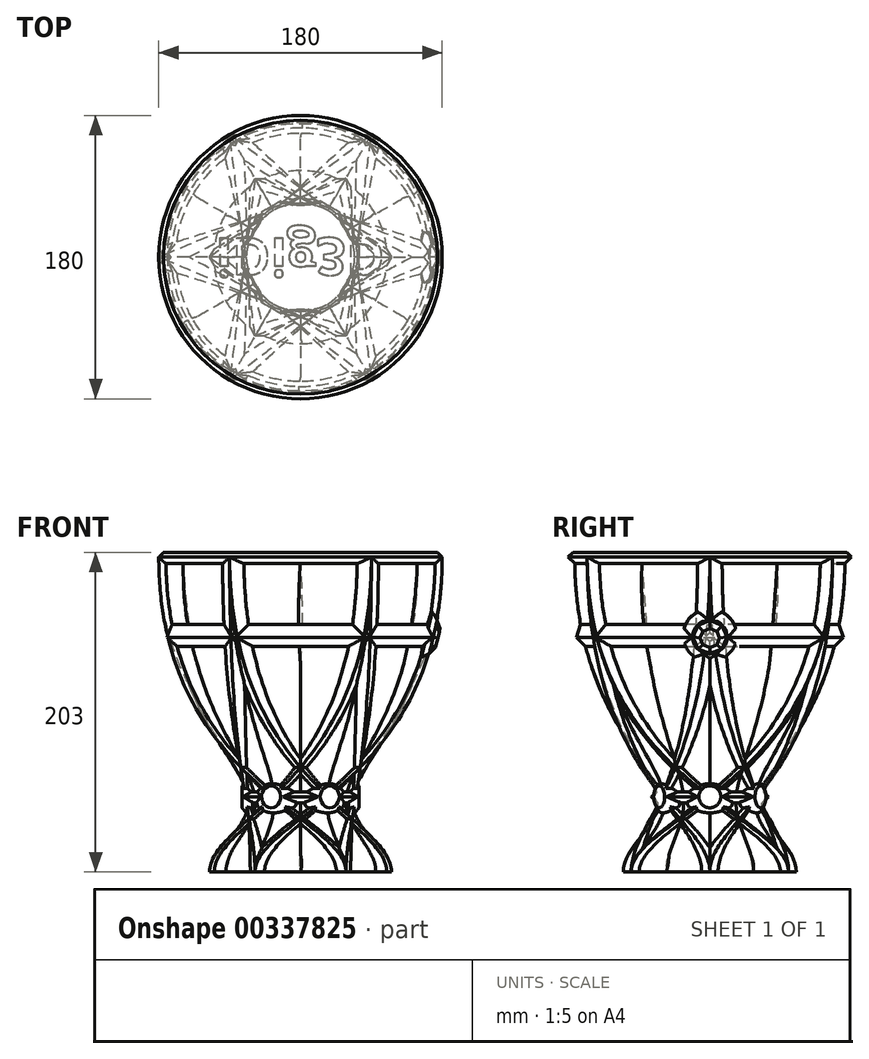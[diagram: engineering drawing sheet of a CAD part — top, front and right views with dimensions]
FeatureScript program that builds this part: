
annotation { "Feature Type Name" : "Feature", "Feature Type Description" : "" }
export const myFeature = defineFeature(function(context is Context, id is Id, definition is map)
    precondition{}
    {
        {
            var Q0;
            Q0=qCreatedBy(makeId("Top.planeOp"),FACE);
            var sketch = newSketch(context, id + "F0", { "sketchPlane" : qUnion([Q0])});
            skCircle(sketch, "E0.cCircle", {"center": v(0, 0) * mm, "radius": 50 * mm, "construction": true});
            skLineSegment(sketch, "E0.0", {"start": v(-28.87, 50) * mm, "end": v(28.87, 50) * mm});
            skLineSegment(sketch, "E0.1", {"start": v(28.87, 50) * mm, "end": v(57.74, 0) * mm});
            skLineSegment(sketch, "E0.2", {"start": v(57.74, 0) * mm, "end": v(28.87, -50) * mm});
            skLineSegment(sketch, "E0.3", {"start": v(28.87, -50) * mm, "end": v(-28.87, -50) * mm});
            skLineSegment(sketch, "E0.4", {"start": v(-28.87, -50) * mm, "end": v(-57.74, 0) * mm});
            skLineSegment(sketch, "E0.5", {"start": v(-57.74, 0) * mm, "end": v(-28.87, 50) * mm});
            skPoint(sketch, "E0.0.midPoint", {"position": v(0, 50) * mm});
            skArc(sketch, "E1", {"start": v(22.87, 50) * mm, "mid": v(0, 54.98) * mm, "end": v(-22.87, 50) * mm});
            skArc(sketch, "E2.1.0", {"start": v(-31.87, 44.8) * mm, "mid": v(-47.62, 27.5) * mm, "end": v(-54.74, 5.2) * mm});
            skArc(sketch, "E2.2.0", {"start": v(-54.74, -5.2) * mm, "mid": v(-47.62, -27.5) * mm, "end": v(-31.87, -44.8) * mm});
            skArc(sketch, "E3.3.3.0", {"start": v(-22.87, -50) * mm, "mid": v(0, -54.98) * mm, "end": v(22.87, -50) * mm});
            skArc(sketch, "E3.3.4.0", {"start": v(31.87, -44.8) * mm, "mid": v(47.62, -27.5) * mm, "end": v(54.74, -5.2) * mm});
            skArc(sketch, "E3.3.5.0", {"start": v(54.74, 5.2) * mm, "mid": v(47.62, 27.5) * mm, "end": v(31.87, 44.8) * mm});
            skSolve(sketch);
        }
        {
            var Q0;
            Q0=qCreatedBy(makeId("Top.planeOp"),FACE);
            cPlane(context, id + "F1", {"entities" : qUnion([Q0]), "cplaneType" : CPlaneType.OFFSET, "offset" : 200 * mm, "width" : 150 * mm, "height" : 150 * mm});
        }
        {
            var Q0;
            Q0=qCreatedBy(id+"F1.planeOp",FACE);
            var sketch = newSketch(context, id + "F2", { "sketchPlane" : qUnion([Q0])});
            skCircle(sketch, "E4.cCircle", {"center": v(0, 0) * mm, "radius": 90 * mm, "construction": true});
            skLineSegment(sketch, "E4.0", {"start": v(-90, 0) * mm, "end": v(-45, 77.94) * mm});
            skLineSegment(sketch, "E4.1", {"start": v(-45, 77.94) * mm, "end": v(45, 77.94) * mm});
            skLineSegment(sketch, "E4.2", {"start": v(45, 77.94) * mm, "end": v(90, 0) * mm});
            skLineSegment(sketch, "E4.3", {"start": v(90, 0) * mm, "end": v(45, -77.94) * mm});
            skLineSegment(sketch, "E4.4", {"start": v(45, -77.94) * mm, "end": v(-45, -77.94) * mm});
            skLineSegment(sketch, "E4.5", {"start": v(-45, -77.94) * mm, "end": v(-90, 0) * mm});
            skCircle(sketch, "E5", {"center": v(0, 0) * mm, "radius": 85.85 * mm});
            skPoint(sketch, "E6", {"position": v(-85.5, 7.8) * mm});
            skSolve(sketch);
        }
        {
            var Q1;
            Q1 = qSketchRegion(id + "F0", true);
            var Q2;
            Q2 = qSketchRegion(id + "F2", true);
            var Q3;
            Q3=sQuery(id+"F0.wireOp",VERTEX,"E0.3.start");
            var Q4;
            Q4=sQuery(id+"F2.wireOp",VERTEX,"E4.0.start");
            loft(context, id + "F3", {"startCondition" : LoftEndDerivativeType.NORMAL_TO_PROFILE, "startMagnitude" : 0.5, "endCondition" : LoftEndDerivativeType.NORMAL_TO_PROFILE, "endMagnitude" : 2.1, "sheetProfilesArray" : [{ "sheetProfileEntities" : qUnion([Q1]) }, { "sheetProfileEntities" : qUnion([Q2]) }], "matchConnections" : true, "connections" : [{ "connectionEntities" : qUnion([Q3, Q4]), "connectionEdgeQueries" : qUnion([]), "connectionEdgeParameters" : [] }]});
        }
        {
            var Q0;
            {var subQ0=sQuery(id+"F2.wireOp",EDGE,"E4.5");var subQ1=sQuery(id+"F2.wireOp",EDGE,"E4.0");var subQ2=makeQuery(id+"F2.imprint","INTERSECT",VERTEX,{"derivedFrom":[subQ1,subQ0]});var subQ6=sQuery(id+"F0.wireOp",EDGE,"E1");Q0=makeQuery(id+"F3.opLoft","SWEPT_BODY",BODY,{"disambiguationData":[OSD([makeQuery(id+"F0.imprint","IMPRINT",FACE,{"disambiguationData":[TD([[makeQuery(id+"F0.imprint","IMPRINT",EDGE,{"derivedFrom":subQ6}),1.0]])]}),makeQuery(id+"F2.imprint","IMPRINT",FACE,{"disambiguationData":[TD([[makeQuery(id+"F2.imprint","IMPRINT",EDGE,{"disambiguationData":[TD([[subQ2,-1.0]])],"derivedFrom":subQ1}),-1.0]])]})])]});}
            var Q1;
            Q1=qCreatedBy(makeId("Front.planeOp"),FACE);
            mirror(context, id + "F4", {"operationType" : NewBodyOperationType.ADD, "entities" : qUnion([Q0]), "mirrorPlane" : qUnion([Q1])});
        }
        {
            var Q0;
            Q0=qCreatedBy(makeId("Front.planeOp"),FACE);
            var sketch = newSketch(context, id + "F5", { "sketchPlane" : qUnion([Q0])});
            skLineSegment(sketch, "E7", {"start": v(80.54, 160.36) * mm, "end": v(84.28, 149.21) * mm, "construction": true});
            skLineSegment(sketch, "E8", {"start": v(84.28, 149.21) * mm, "end": v(75.96, 140.9) * mm, "construction": true});
            skLineSegment(sketch, "E9", {"start": v(75.96, 140.9) * mm, "end": v(0, 158.76) * mm});
            skLineSegment(sketch, "E10", {"start": v(0, 179.3) * mm, "end": v(80.54, 160.36) * mm});
            skLineSegment(sketch, "E11", {"start": v(80, 210) * mm, "end": v(90, 200) * mm});
            skLineSegment(sketch, "E12", {"start": v(80, 190) * mm, "end": v(0, 190) * mm});
            skLineSegment(sketch, "E13", {"start": v(0, 210) * mm, "end": v(80, 210) * mm, "construction": true});
            skLineSegment(sketch, "E14", {"start": v(28.17, 56.78) * mm, "end": v(37.17, 47.78) * mm});
            skLineSegment(sketch, "E15", {"start": v(37.17, 47.78) * mm, "end": v(28.17, 38.78) * mm});
            skLineSegment(sketch, "E16", {"start": v(28.17, 38.78) * mm, "end": v(0, 38.78) * mm});
            skLineSegment(sketch, "E17", {"start": v(0, 56.78) * mm, "end": v(28.17, 56.78) * mm});
            skLineSegment(sketch, "E18.0", {"start": v(84.74, 149.1) * mm, "end": v(75.79, 140.16) * mm});
            skLineSegment(sketch, "E18.1", {"start": v(80.71, 161.1) * mm, "end": v(84.74, 149.1) * mm});
            skLineSegment(sketch, "E19", {"start": v(80.54, 160.36) * mm, "end": v(80.71, 161.1) * mm});
            skLineSegment(sketch, "E20", {"start": v(75.96, 140.9) * mm, "end": v(75.79, 140.16) * mm});
            skPoint(sketch, "E21.orphan", {"position": v(90, 200) * mm});
            skLineSegment(sketch, "E22", {"start": v(80.27, 150.15) * mm, "end": v(84.74, 149.1) * mm, "construction": true});
            skPoint(sketch, "E23.0", {"position": v(0, 247.2) * mm});
            skLineSegment(sketch, "E24", {"start": v(87, 203) * mm, "end": v(0, 203) * mm});
            skFitSpline(sketch, "E25.0", {"points": [v(-28.87, 0) * mm, v(-28.87, 33.97) * mm, v(90, 57.34) * mm, v(90, 200) * mm], "construction": true});
            skPoint(sketch, "E26.0", {"position": v(17.59, 47.78) * mm});
            skPoint(sketch, "E26.1", {"position": v(35.17, 47.78) * mm});
            skFitSpline(sketch, "E27.0", {"points": [v(85.85, 198.7) * mm, v(85.82, 195.76) * mm, v(85.67, 189.89) * mm, v(85.12, 181.1) * mm, v(84.24, 172.34) * mm, v(83.22, 165.08) * mm, v(82.21, 159.3) * mm, v(81.08, 153.56) * mm, v(79.76, 147.86) * mm, v(78.24, 142.2) * mm, v(76.59, 136.6) * mm, v(74.73, 131.06) * mm, v(72.67, 125.59) * mm, v(70.48, 120.19) * mm, v(68.1, 114.88) * mm, v(65.5, 109.67) * mm, v(62.77, 104.54) * mm, v(59.86, 99.54) * mm, v(56.76, 94.64) * mm, v(53.54, 89.84) * mm, v(50.15, 85.17) * mm, v(46.6, 80.63) * mm, v(42.93, 76.2) * mm, v(40.07, 72.97) * mm, v(38.12, 70.87) * mm], "construction": true});
            skLineSegment(sketch, "E28", {"start": v(90, 200) * mm, "end": v(80, 190) * mm});
            skLineSegment(sketch, "E29", {"start": v(0, 190) * mm, "end": v(0, 210) * mm});
            skLineSegment(sketch, "E30", {"start": v(0, 158.76) * mm, "end": v(0, 179.3) * mm});
            skLineSegment(sketch, "E31", {"start": v(0, 38.78) * mm, "end": v(0, 56.78) * mm});
            skPoint(sketch, "E32.0", {"position": v(85.5, 200) * mm});
            skPoint(sketch, "E33.0", {"position": v(38.93, 71.75) * mm});
            skFitSpline(sketch, "E34.0.1", {"points": [v(85.5, 200) * mm, v(81.78, 200) * mm, v(78.07, 200) * mm, v(74.35, 200) * mm]});
            skFitSpline(sketch, "E34.2", {"points": [v(85.5, 200) * mm, v(85.5, 197.06) * mm, v(85.4, 191.2) * mm, v(84.94, 182.4) * mm, v(84.13, 173.64) * mm, v(83.17, 166.37) * mm, v(82.22, 160.58) * mm, v(81.14, 154.83) * mm, v(79.87, 149.11) * mm, v(78.4, 143.44) * mm, v(76.8, 137.82) * mm, v(75, 132.27) * mm, v(72.99, 126.78) * mm, v(70.85, 121.36) * mm, v(68.5, 116.03) * mm, v(65.96, 110.8) * mm, v(63.28, 105.65) * mm, v(60.41, 100.61) * mm, v(57.35, 95.7) * mm, v(54.18, 90.86) * mm, v(50.83, 86.16) * mm, v(47.31, 81.59) * mm, v(43.7, 77.11) * mm, v(40.87, 73.87) * mm, v(38.93, 71.75) * mm], "construction": true});
            skSolve(sketch);
        }
        {
            var Q0;
            {var subQ3=sQuery(id+"F5.wireOp",EDGE,"E12");Q0=makeQuery(id+"F5.imprint","IMPRINT",FACE,{"disambiguationData":[TD([[makeQuery(id+"F5.imprint","IMPRINT",EDGE,{"derivedFrom":subQ3}),-1.0]])]});}
            var Q1;
            Q1=makeQuery(id+"F5.imprint","IMPRINT",FACE,{"disambiguationData":[TD([[makeQuery(id+"F5.imprint","IMPRINT",EDGE,{"derivedFrom":sQuery(id+"F5.wireOp",EDGE,"E9")}),-1.0]])]});
            var Q2;
            Q2=makeQuery(id+"F5.imprint","IMPRINT",FACE,{"disambiguationData":[TD([[makeQuery(id+"F5.imprint","IMPRINT",EDGE,{"derivedFrom":sQuery(id+"F5.wireOp",EDGE,"E14")}),-1.0]])]});
            var Q3;
            Q3=sQuery(id+"F5.wireOp",EDGE,"E31");
            revolve(context, id + "F6", {"operationType" : NewBodyOperationType.ADD, "entities" : qUnion([Q0, Q1, Q2]), "axis" : qUnion([Q3]), "revolveType" : RevolveType.FULL});
        }
        {
            var Q0;
            Q0=qCreatedBy(makeId("Right.planeOp"),FACE);
            var Q1;
            Q1=sQuery(id+"F5.wireOp",VERTEX,"E15.start");
            cPlane(context, id + "F7", {"entities" : qUnion([Q0, Q1]), "cplaneType" : CPlaneType.PLANE_POINT, "offset" : 25 * mm, "width" : 150 * mm, "height" : 150 * mm});
        }
        {
            var Q0;
            Q0=qCreatedBy(id+"F7.planeOp",FACE);
            var sketch = newSketch(context, id + "F8", { "sketchPlane" : qUnion([Q0])});
            skLineSegment(sketch, "E35.0", {"start": v(37.17, 47.78) * mm, "end": v(-37.17, 47.78) * mm, "construction": true});
            skCircle(sketch, "E36.cCircle", {"center": v(0, 47.78) * mm, "radius": 15 * mm});
            skSolve(sketch);
        }
        {
            var Q0;
            Q0=qSketchRegion(id+"F8",true);
            extrude(context, id + "F9", {"entities" : qUnion([Q0]), "oppositeDirection" : true, "depth" : 25 * mm});
        }
        {
            var Q0;
            Q0=makeQuery(id+"F9.opExtrude","CAP_FACE",FACE,{"disambiguationData":[OSD([sQuery(id+"F8.wireOp",EDGE,"E36.cCircle")])],"isStart":true});
            chamfer(context, id + "F10", {"entities" : qUnion([Q0]), "chamferType" : ChamferType.OFFSET_ANGLE, "width" : 8 * mm, "oppositeDirection" : false, "angle" : 40 * degree, "tangentPropagation" : true});
        }
        {
            var Q0;
            Q0=sQuery(id+"F5.wireOp",VERTEX,"E18.1.end");
            var Q1;
            Q1=sQuery(id+"F5.wireOp",EDGE,"E22");
            cPlane(context, id + "F11", {"entities" : qUnion([Q0, Q1]), "cplaneType" : CPlaneType.LINE_POINT, "offset" : 25 * mm, "width" : 150 * mm, "height" : 150 * mm});
        }
        {
            var Q0;
            Q0=qCreatedBy(id+"F11.planeOp",FACE);
            var sketch = newSketch(context, id + "F12", { "sketchPlane" : qUnion([Q0])});
            skCircle(sketch, "E37", {"center": v(0, 164.54) * mm, "radius": 9.02 * mm, "construction": true});
            skPoint(sketch, "E38.0", {"position": v(9.02, 171.6) * mm});
            skPoint(sketch, "E38.1", {"position": v(-9.02, 171.6) * mm});
            skLineSegment(sketch, "E39", {"start": v(-9.02, 171.6) * mm, "end": v(9.02, 171.6) * mm, "construction": true});
            skLineSegment(sketch, "E40", {"start": v(-9.02, 164.54) * mm, "end": v(9.02, 164.54) * mm, "construction": true});
            skCircle(sketch, "E41.0", {"center": v(0, 164.54) * mm, "radius": 17.02 * mm});
            skSolve(sketch);
        }
        {
            var Q0;
            Q0=qSketchRegion(id+"F12",true);
            extrude(context, id + "F13", {"entities" : qUnion([Q0]), "oppositeDirection" : true, "depth" : 25 * mm, "hasSecondDirection" : true, "secondDirectionOppositeDirection" : true, "secondDirectionDepth" : .5 * mm});
        }
        {
            var Q0;
            Q0=makeQuery(id+"F13.opExtrude","CAP_FACE",FACE,{"disambiguationData":[OSD([sQuery(id+"F12.wireOp",EDGE,"E41.0")])],"isStart":true});
            chamfer(context, id + "F14", {"entities" : qUnion([Q0]), "chamferType" : ChamferType.OFFSET_ANGLE, "width" : 6 * mm, "oppositeDirection" : false, "angle" : 35 * degree, "tangentPropagation" : true});
        }
        {
            var Q0;
            Q0=makeQuery(id+"F13.opExtrude","CAP_FACE",FACE,{"disambiguationData":[OSD([sQuery(id+"F12.wireOp",EDGE,"E41.0")])],"isStart":true});
            var sketch = newSketch(context, id + "F15", { "sketchPlane" : qUnion([Q0])});
            skCircle(sketch, "E42.0", {"center": v(0, 164.54) * mm, "radius": 11.02 * mm, "construction": true});
            skCircle(sketch, "E43.0", {"center": v(0, 164.54) * mm, "radius": 10.82 * mm, "construction": true});
            skLineSegment(sketch, "E44.0", {"start": v(0, 175.36) * mm, "end": v(7.65, 172.2) * mm});
            skLineSegment(sketch, "E44.1", {"start": v(7.65, 172.2) * mm, "end": v(10.82, 164.54) * mm});
            skLineSegment(sketch, "E44.2", {"start": v(10.82, 164.54) * mm, "end": v(7.65, 156.9) * mm});
            skLineSegment(sketch, "E44.3", {"start": v(7.65, 156.9) * mm, "end": v(0, 153.73) * mm});
            skLineSegment(sketch, "E44.4", {"start": v(0, 153.73) * mm, "end": v(-7.65, 156.9) * mm});
            skLineSegment(sketch, "E44.5", {"start": v(-7.65, 156.9) * mm, "end": v(-10.82, 164.54) * mm});
            skLineSegment(sketch, "E44.6", {"start": v(-10.82, 164.54) * mm, "end": v(-7.65, 172.2) * mm});
            skLineSegment(sketch, "E44.7", {"start": v(-7.65, 172.2) * mm, "end": v(0, 175.36) * mm});
            skSolve(sketch);
        }
        {
            var Q0;
            Q0=qSketchRegion(id+"F15",true);
            extrude(context, id + "F16", {"entities" : qUnion([Q0]), "operationType" : NewBodyOperationType.ADD, "depth" : 3 * mm, "hasDraft" : true, "draftAngle" : 55 * degree, "draftPullDirection" : true});
        }
        {
            var Q0;
            Q0=makeQuery(id+"F13.opExtrude","SWEPT_BODY",BODY,{"disambiguationData":[OSD([sQuery(id+"F12.wireOp",EDGE,"E41.0")])]});
            var Q1;
            Q1=makeQuery(id+"F9.opExtrude","SWEPT_BODY",BODY,{"disambiguationData":[OSD([sQuery(id+"F8.wireOp",EDGE,"E36.cCircle")])]});
            var Q2;
            Q2=makeQuery(id+"F14.opChamfer","BLEND_FACE",FACE,{"disambiguationData":[OSD([sQuery(id+"F12.wireOp",EDGE,"E41.0")])]});
            var Q3;
            {var subQ0=sQuery(id+"F15.wireOp",EDGE,"E44.2");var subQ1=sQuery(id+"F15.wireOp",EDGE,"E44.1");var subQ2=sQuery(id+"F15.wireOp",EDGE,"E44.3");var subQ3=sQuery(id+"F15.wireOp",EDGE,"E44.0");var subQ4=sQuery(id+"F15.wireOp",EDGE,"E44.4");var subQ5=sQuery(id+"F15.wireOp",EDGE,"E44.5");var subQ6=sQuery(id+"F15.wireOp",EDGE,"E44.6");var subQ7=sQuery(id+"F15.wireOp",EDGE,"E44.7");Q3=makeQuery(id+"F16.boolean.opBoolean","COPY",FACE,{"disambiguationData":[TD([makeQuery(id+"F16.opExtrude","SWEPT_FACE",FACE,{"disambiguationData":[OSD([subQ3])]})])],"derivedFrom":makeQuery(id+"F16.opExtrude","CAP_FACE",FACE,{"disambiguationData":[OSD([subQ3,subQ1,subQ0,subQ2,subQ4,subQ5,subQ6,subQ7])],"isStart":false})});}
            var Q4;
            Q4=makeQuery(id+"F16.boolean.opBoolean","COPY",FACE,{"derivedFrom":makeQuery(id+"F16.opExtrude","SWEPT_FACE",FACE,{"disambiguationData":[OSD([sQuery(id+"F15.wireOp",EDGE,"E44.7")])]})});
            var Q5;
            Q5=makeQuery(id+"F16.boolean.opBoolean","COPY",FACE,{"derivedFrom":makeQuery(id+"F16.opExtrude","SWEPT_FACE",FACE,{"disambiguationData":[OSD([sQuery(id+"F15.wireOp",EDGE,"E44.0")])]})});
            var Q6;
            {var subQ1=sQuery(id+"F15.wireOp",EDGE,"E44.1");Q6=makeQuery(id+"F16.boolean.opBoolean","COPY",FACE,{"disambiguationData":[TD([makeQuery(id+"F14.opChamfer","BLEND_FACE",FACE,{"disambiguationData":[OSD([sQuery(id+"F12.wireOp",EDGE,"E41.0")])]})])],"derivedFrom":makeQuery(id+"F16.opExtrude","SWEPT_FACE",FACE,{"disambiguationData":[OSD([subQ1])]})});}
            var Q7;
            {var subQ1=sQuery(id+"F15.wireOp",EDGE,"E44.2");Q7=makeQuery(id+"F16.boolean.opBoolean","COPY",FACE,{"disambiguationData":[TD([makeQuery(id+"F14.opChamfer","BLEND_FACE",FACE,{"disambiguationData":[OSD([sQuery(id+"F12.wireOp",EDGE,"E41.0")])]})])],"derivedFrom":makeQuery(id+"F16.opExtrude","SWEPT_FACE",FACE,{"disambiguationData":[OSD([subQ1])]})});}
            var Q8;
            Q8=makeQuery(id+"F16.boolean.opBoolean","COPY",FACE,{"derivedFrom":makeQuery(id+"F16.opExtrude","SWEPT_FACE",FACE,{"disambiguationData":[OSD([sQuery(id+"F15.wireOp",EDGE,"E44.3")])]})});
            var Q9;
            Q9=makeQuery(id+"F16.boolean.opBoolean","COPY",FACE,{"derivedFrom":makeQuery(id+"F16.opExtrude","SWEPT_FACE",FACE,{"disambiguationData":[OSD([sQuery(id+"F15.wireOp",EDGE,"E44.4")])]})});
            var Q10;
            {var subQ1=sQuery(id+"F15.wireOp",EDGE,"E44.5");Q10=makeQuery(id+"F16.boolean.opBoolean","COPY",FACE,{"disambiguationData":[TD([makeQuery(id+"F14.opChamfer","BLEND_FACE",FACE,{"disambiguationData":[OSD([sQuery(id+"F12.wireOp",EDGE,"E41.0")])]})])],"derivedFrom":makeQuery(id+"F16.opExtrude","SWEPT_FACE",FACE,{"disambiguationData":[OSD([subQ1])]})});}
            var Q11;
            {var subQ1=sQuery(id+"F15.wireOp",EDGE,"E44.6");Q11=makeQuery(id+"F16.boolean.opBoolean","COPY",FACE,{"disambiguationData":[TD([makeQuery(id+"F14.opChamfer","BLEND_FACE",FACE,{"disambiguationData":[OSD([sQuery(id+"F12.wireOp",EDGE,"E41.0")])]})])],"derivedFrom":makeQuery(id+"F16.opExtrude","SWEPT_FACE",FACE,{"disambiguationData":[OSD([subQ1])]})});}
            var Q12;
            Q12=makeQuery(id+"F10.opChamfer","BLEND_FACE",FACE,{"disambiguationData":[OSD([sQuery(id+"F8.wireOp",EDGE,"E36.cCircle")])]});
            var Q13;
            Q13=makeQuery(id+"F9.opExtrude","CAP_FACE",FACE,{"disambiguationData":[OSD([sQuery(id+"F8.wireOp",EDGE,"E36.cCircle")])],"isStart":true});
            var Q14;
            Q14=sQuery(id+"F5.wireOp",EDGE,"E31");
            circularPattern(context, id + "F17", {"operationType" : NewBodyOperationType.ADD, "entities" : qUnion([Q0, Q1]), "axis" : qUnion([Q14]), "angle" : 360 * degree, "instanceCount" : 6, "equalSpace" : true});
        }
        {
            var Q0;
            {var subQ13=sQuery(id+"F0.wireOp",EDGE,"E0.5");var subQ14=sQuery(id+"F0.wireOp",EDGE,"E0.0");var subQ15=makeQuery(id+"F0.imprint","INTERSECT",VERTEX,{"derivedFrom":[subQ14,subQ13]});Q0=makeQuery(id+"F3.opLoft","CAP_FACE",FACE,{"disambiguationData":[OSD([makeQuery(id+"F0.imprint","IMPRINT",FACE,{"disambiguationData":[TD([[makeQuery(id+"F0.imprint","IMPRINT",EDGE,{"disambiguationData":[TD([[subQ15,-1.0]])],"derivedFrom":subQ14}),-1.0]])]})])],"isStart":true});}
            var sketch = newSketch(context, id + "F18", { "sketchPlane" : qUnion([Q0])});
            skText(sketch, "E45", { "text": "iDig3D", "fontName": "OpenSans-Bold.ttf"});
            const initialGuessF18  = {"E45": [-0.05358, -0.01233, 1, 0, 0.0239]};
            skSetInitialGuess(sketch, initialGuessF18);
            skSolve(sketch);
        }
        {
            var Q0;
            Q0=qSketchRegion(id+"F18",true);
            extrude(context, id + "F19", {"entities" : qUnion([Q0]), "operationType" : NewBodyOperationType.REMOVE, "oppositeDirection" : true, "depth" : .25 * mm, "hasDraft" : true, "draftAngle" : 30 * degree, "draftPullDirection" : true});
        }
    });
